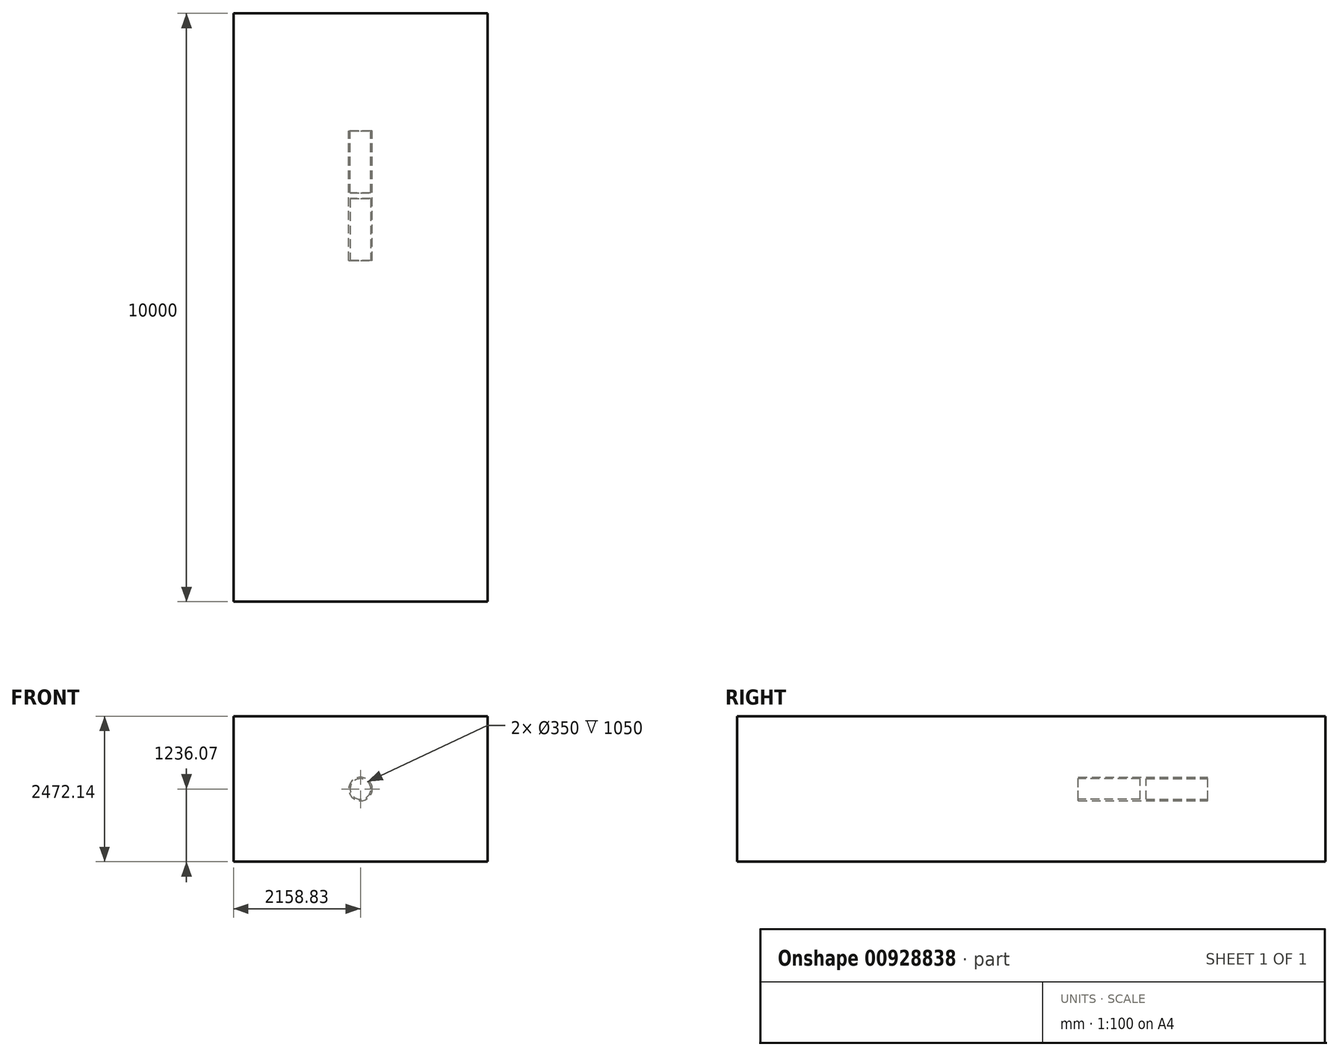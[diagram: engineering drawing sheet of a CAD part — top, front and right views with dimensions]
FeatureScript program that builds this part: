
annotation { "Feature Type Name" : "Feature", "Feature Type Description" : "" }
export const myFeature = defineFeature(function(context is Context, id is Id, definition is map)
    precondition{}
    {
        {
            var Q0;
            Q0=qCreatedBy(makeId("Front.planeOp"),FACE);
            var sketch = newSketch(context, id + "F0", { "sketchPlane" : qUnion([Q0])});
            skCircle(sketch, "E0", {"center": v(0, 0) * mm, "radius": 200 * mm});
            skSolve(sketch);
        }
        {
            var Q0;
            Q0 = qSketchRegion(id + "F0", true);
            extrude(context, id + "F1", {"entities" : qUnion([Q0]), "depth" : 2200 * mm, "offsetDistance" : 25 * mm});
        }
        {
            var Q0;
            Q0=qCreatedBy(makeId("Front.planeOp"),FACE);
            var sketch = newSketch(context, id + "F2", { "sketchPlane" : qUnion([Q0])});
            skCircle(sketch, "E1", {"center": v(0, 0) * mm, "radius": 175 * mm});
            skSolve(sketch);
        }
        {
            var Q0;
            Q0 = qSketchRegion(id + "F2", true);
            extrude(context, id + "F3", {"entities" : qUnion([Q0]), "operationType" : NewBodyOperationType.REMOVE, "depth" : 1050 * mm, "offsetDistance" : 25 * mm});
        }
        {
            var Q0;
            Q0=makeQuery(id+"F1.opExtrude","CAP_FACE",FACE,{"disambiguationData":[OSD([sQuery(id+"F0.wireOp",EDGE,"E0")])],"isStart":false});
            var sketch = newSketch(context, id + "F4", { "sketchPlane" : qUnion([Q0])});
            skCircle(sketch, "E2", {"center": v(0, 0) * mm, "radius": 175 * mm});
            skSolve(sketch);
        }
        {
            var Q0;
            Q0 = qSketchRegion(id + "F4", true);
            extrude(context, id + "F5", {"entities" : qUnion([Q0]), "operationType" : NewBodyOperationType.REMOVE, "oppositeDirection" : true, "depth" : 1050 * mm, "offsetDistance" : 25 * mm});
        }
        {
            var Q0;
            Q0=qCreatedBy(makeId("Front.planeOp"),FACE);
            cPlane(context, id + "F6", {"entities" : qUnion([Q0]), "cplaneType" : CPlaneType.OFFSET, "offset" : 2000 * mm, "oppositeDirection" : true, "width" : 150 * mm, "height" : 150 * mm});
        }
        {
            var Q0;
            Q0=qCreatedBy(id+"F6.planeOp",FACE);
            var sketch = newSketch(context, id + "F7", { "sketchPlane" : qUnion([Q0])});
            skLineSegment(sketch, "E3.bottom", {"start": v(-2158.83, 1236.07) * mm, "end": v(2158.83, 1236.07) * mm});
            skLineSegment(sketch, "E3.top", {"start": v(-2158.83, -1236.07) * mm, "end": v(2158.83, -1236.07) * mm});
            skLineSegment(sketch, "E3.left", {"start": v(-2158.83, 1236.07) * mm, "end": v(-2158.83, -1236.07) * mm});
            skLineSegment(sketch, "E3.right", {"start": v(2158.83, 1236.07) * mm, "end": v(2158.83, -1236.07) * mm});
            skPoint(sketch, "E3.middle", {"position": v(0, 0) * mm});
            skSolve(sketch);
        }
        {
            var Q0;
            Q0 = qSketchRegion(id + "F7", true);
            extrude(context, id + "F8", {"entities" : qUnion([Q0]), "depth" : 10000 * mm, "offsetDistance" : 25 * mm});
        }
    });
